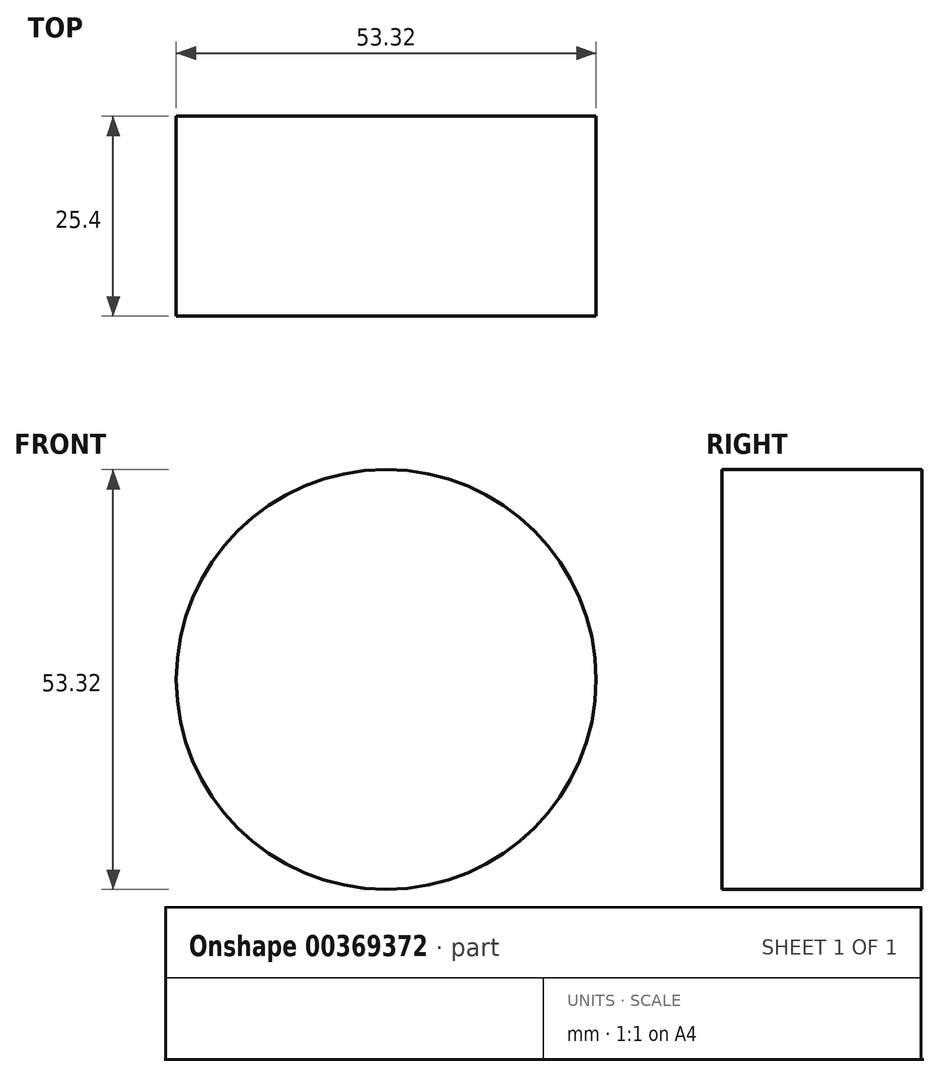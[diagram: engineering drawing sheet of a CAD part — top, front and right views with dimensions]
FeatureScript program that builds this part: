
annotation { "Feature Type Name" : "Feature", "Feature Type Description" : "" }
export const myFeature = defineFeature(function(context is Context, id is Id, definition is map)
    precondition{}
    {
        {
            var Q0;
            Q0=qCreatedBy(makeId("Front.planeOp"),FACE);
            var sketch = newSketch(context, id + "F0", { "sketchPlane" : qUnion([Q0])});
            skCircle(sketch, "E0", {"center": v(-28.48, 28.33) * mm, "radius": 26.66 * mm});
            skSolve(sketch);
        }
        {
            var Q0;
            Q0 = qSketchRegion(id + "F0", true);
            extrude(context, id + "F1", {"entities" : qUnion([Q0]), "depth" : 25.4 * mm});
        }
    });
